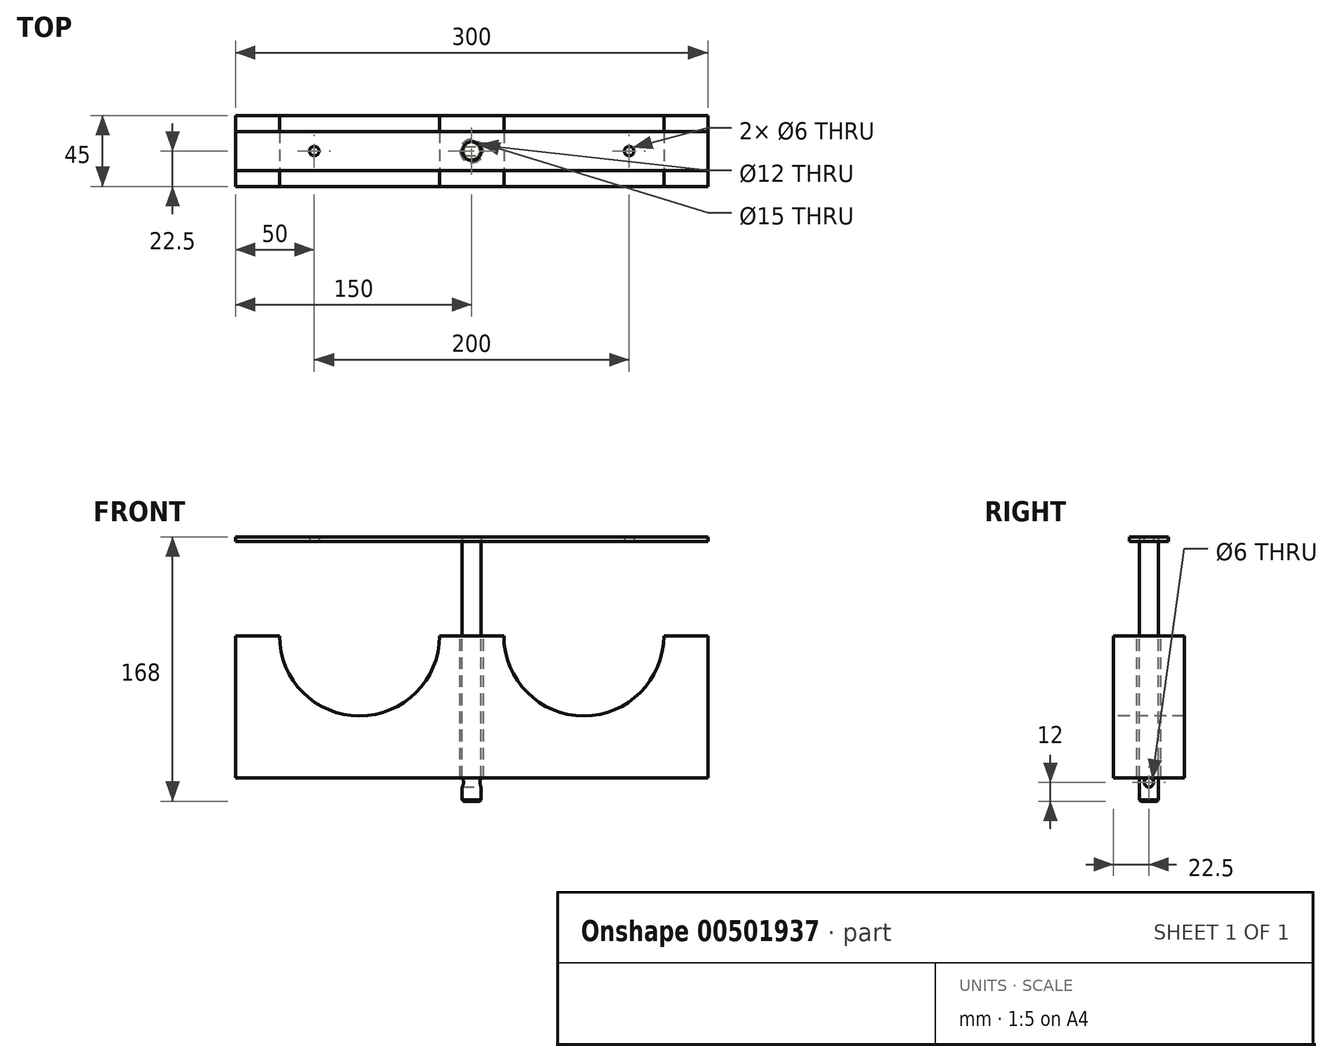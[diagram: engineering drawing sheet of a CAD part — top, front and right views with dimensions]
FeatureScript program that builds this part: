
annotation { "Feature Type Name" : "Feature", "Feature Type Description" : "" }
export const myFeature = defineFeature(function(context is Context, id is Id, definition is map)
    precondition{}
    {
        {
            var Q0;
            Q0=qCreatedBy(makeId("Front.planeOp"),FACE);
            var sketch = newSketch(context, id + "F0", { "sketchPlane" : qUnion([Q0])});
            skLineSegment(sketch, "E0.bottom", {"start": v(150, 45) * mm, "end": v(122.05, 45) * mm});
            skLineSegment(sketch, "E0.top", {"start": v(150, -45) * mm, "end": v(-150, -45) * mm});
            skLineSegment(sketch, "E0.left", {"start": v(150, 45) * mm, "end": v(150, -45) * mm});
            skLineSegment(sketch, "E0.right", {"start": v(-150, 45) * mm, "end": v(-150, -45) * mm});
            skPoint(sketch, "E0.middle", {"position": v(0, 0) * mm});
            skLineSegment(sketch, "E1", {"start": v(0, 45) * mm, "end": v(0, -45) * mm, "construction": true});
            skLineSegment(sketch, "E2", {"start": v(-150, 0) * mm, "end": v(150, 0) * mm, "construction": true});
            skPoint(sketch, "E2.endSnap0", {"position": v(150, 0) * mm});
            skArc(sketch, "E3", {"start": v(-122.05, 45) * mm, "mid": v(-71.25, -5.8) * mm, "end": v(-20.45, 45) * mm});
            skLineSegment(sketch, "E4.trimOffspring", {"start": v(-122.05, 45) * mm, "end": v(-150, 45) * mm});
            skArc(sketch, "E5.MirrorCS", {"start": v(122.05, 45) * mm, "mid": v(71.25, -5.8) * mm, "end": v(20.45, 45) * mm});
            skLineSegment(sketch, "E6.trimOffspring", {"start": v(20.45, 45) * mm, "end": v(-20.45, 45) * mm});
            skSolve(sketch);
        }
        {
            var Q0;
            Q0 = qSketchRegion(id + "F0", true);
            extrude(context, id + "F1", {"entities" : qUnion([Q0]), "oppositeDirection" : true, "depth" : 45 * mm});
        }
        {
            var Q0;
            Q0=makeQuery(id+"F1.opExtrude","SWEPT_FACE",FACE,{"disambiguationData":[OSD([sQuery(id+"F0.wireOp",EDGE,"E6.trimOffspring")])]});
            var sketch = newSketch(context, id + "F2", { "sketchPlane" : qUnion([Q0])});
            skCircle(sketch, "E7", {"center": v(0, 22.5) * mm, "radius": 7.5 * mm});
            skPoint(sketch, "E7.centerSnap0", {"position": v(-20.45, 22.5) * mm});
            skPoint(sketch, "E7.centerSnap1", {"position": v(0, 45) * mm});
            skSolve(sketch);
        }
        {
            var Q0;
            Q0 = qSketchRegion(id + "F2", true);
            extrude(context, id + "F3", {"entities" : qUnion([Q0]), "operationType" : NewBodyOperationType.REMOVE, "endBound" : BoundingType.THROUGH_ALL, "oppositeDirection" : true, "depth" : 25 * mm});
        }
        {
            var Q0;
            Q0=makeQuery(id+"F1.opExtrude","SWEPT_FACE",FACE,{"disambiguationData":[OSD([sQuery(id+"F0.wireOp",EDGE,"E0.top")])]});
            var sketch = newSketch(context, id + "F4", { "sketchPlane" : qUnion([Q0])});
            skCircle(sketch, "E8.0", {"center": v(0, -22.5) * mm, "radius": 6 * mm});
            skSolve(sketch);
        }
        {
            var Q0;
            Q0 = qSketchRegion(id + "F4", true);
            extrude(context, id + "F5", {"entities" : qUnion([Q0]), "depth" : 15 * mm, "hasSecondDirection" : true, "secondDirectionOppositeDirection" : true, "secondDirectionDepth" : 150 * mm});
        }
        {
            var Q0;
            Q0=makeQuery(id+"F5.opExtrude","CAP_FACE",FACE,{"disambiguationData":[OSD([sQuery(id+"F4.wireOp",EDGE,"E8.0")])],"isStart":true});
            var sketch = newSketch(context, id + "F6", { "sketchPlane" : qUnion([Q0])});
            skLineSegment(sketch, "E9.0", {"start": v(150, 10) * mm, "end": v(-150, 10) * mm});
            skLineSegment(sketch, "E10.0", {"start": v(-150, 35) * mm, "end": v(-150, 10) * mm});
            skLineSegment(sketch, "E11.0", {"start": v(150, 35) * mm, "end": v(150, 10) * mm});
            skLineSegment(sketch, "E12.0", {"start": v(150, 35) * mm, "end": v(-150, 35) * mm});
            skCircle(sketch, "E13", {"center": v(-100, 22.5) * mm, "radius": 3 * mm});
            skPoint(sketch, "E13.centerSnap0", {"position": v(-150, 22.5) * mm});
            skLineSegment(sketch, "E14", {"start": v(0, 35) * mm, "end": v(0, 0) * mm, "construction": true});
            skCircle(sketch, "E15.MirrorC", {"center": v(100, 22.5) * mm, "radius": 3 * mm});
            skCircle(sketch, "E16.0", {"center": v(0, 22.5) * mm, "radius": 6 * mm});
            skSolve(sketch);
        }
        {
            var Q0;
            Q0 = qSketchRegion(id + "F6", true);
            extrude(context, id + "F7", {"entities" : qUnion([Q0]), "depth" : 3 * mm});
        }
        {
            var Q0;
            Q0=qCreatedBy(makeId("Right.planeOp"),FACE);
            var sketch = newSketch(context, id + "F8", { "sketchPlane" : qUnion([Q0])});
            skCircle(sketch, "E17", {"center": v(22.5, -48) * mm, "radius": 3 * mm});
            skSolve(sketch);
        }
        {
            var Q0;
            Q0 = qSketchRegion(id + "F8", true);
            extrude(context, id + "F9", {"entities" : qUnion([Q0]), "operationType" : NewBodyOperationType.REMOVE, "endBound" : BoundingType.SYMMETRIC, "oppositeDirection" : true, "depth" : 25 * mm});
        }
        {
            var Q0;
            Q0=makeQuery(id+"F5.opExtrude","CAP_EDGE",EDGE,{"disambiguationData":[OSD([sQuery(id+"F4.wireOp",EDGE,"E8.0")])],"isStart":false});
            chamfer(context, id + "F10", {"entities" : qUnion([Q0]), "width" : 1 * mm, "tangentPropagation" : true});
        }
    });
